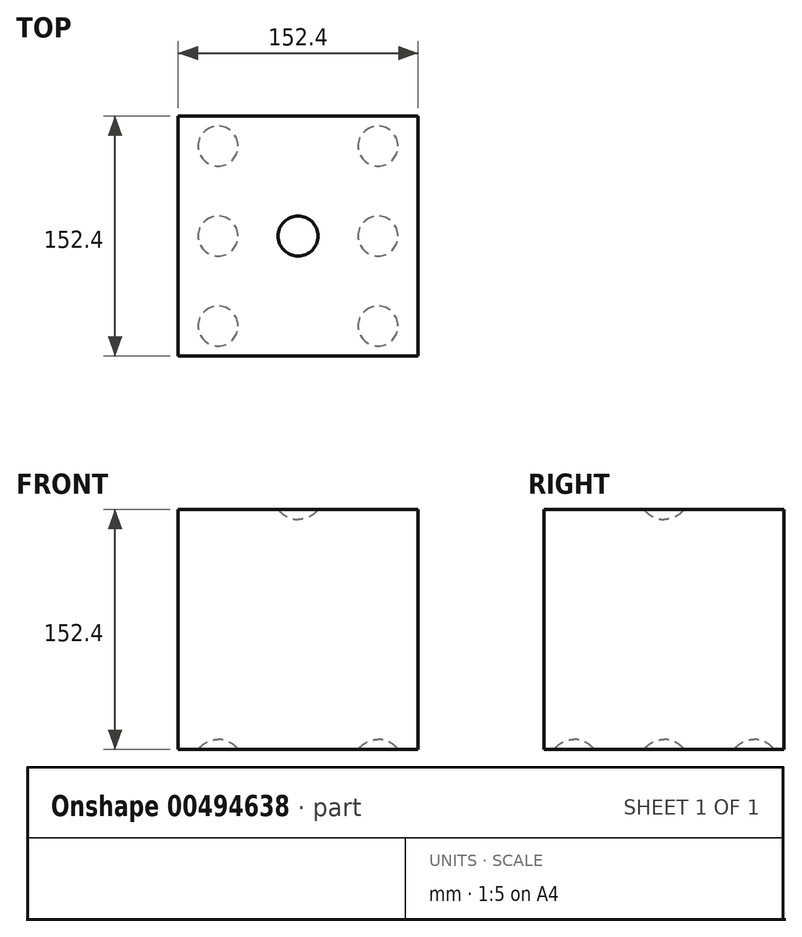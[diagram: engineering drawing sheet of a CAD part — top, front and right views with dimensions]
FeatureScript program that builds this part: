
annotation { "Feature Type Name" : "Feature", "Feature Type Description" : "" }
export const myFeature = defineFeature(function(context is Context, id is Id, definition is map)
    precondition{}
    {
        {
            var Q0;
            Q0=qCreatedBy(makeId("Front.planeOp"),FACE);
            var sketch = newSketch(context, id + "F0", { "sketchPlane" : qUnion([Q0])});
            skLineSegment(sketch, "E0.bottom", {"start": v(76.2, 76.2) * mm, "end": v(-76.2, 76.2) * mm});
            skLineSegment(sketch, "E0.top", {"start": v(76.2, -76.2) * mm, "end": v(-76.2, -76.2) * mm});
            skLineSegment(sketch, "E0.left", {"start": v(76.2, 76.2) * mm, "end": v(76.2, -76.2) * mm});
            skLineSegment(sketch, "E0.right", {"start": v(-76.2, 76.2) * mm, "end": v(-76.2, -76.2) * mm});
            skPoint(sketch, "E0.middle", {"position": v(0, 0) * mm});
            skSolve(sketch);
        }
        {
            var Q0;
            Q0=makeQuery(id+"F0.imprint","IMPRINT",FACE,{"disambiguationData":[TD([[makeQuery(id+"F0.imprint","IMPRINT",EDGE,{"derivedFrom":sQuery(id+"F0.wireOp",EDGE,"E0.bottom")}),1.0]])]});
            extrude(context, id + "F1", {"entities" : qUnion([Q0]), "depth" : 152.4 * mm});
        }
        {
            var Q0;
            Q0=makeQuery(id+"F1.opExtrude","SWEPT_FACE",FACE,{"disambiguationData":[OSD([sQuery(id+"F0.wireOp",EDGE,"E0.bottom")])]});
            var sketch = newSketch(context, id + "F2", { "sketchPlane" : qUnion([Q0])});
            skCircle(sketch, "E1", {"center": v(0, -76.2) * mm, "radius": 12.7 * mm});
            skPoint(sketch, "E1.centerSnap0", {"position": v(76.2, -76.2) * mm});
            skSolve(sketch);
        }
        {
            var Q0;
            Q0=makeQuery(id+"F2.imprint","IMPRINT",FACE,{"disambiguationData":[TD([[makeQuery(id+"F2.imprint","IMPRINT",EDGE,{"derivedFrom":sQuery(id+"F2.wireOp",EDGE,"E1")}),1.0]])]});
            extrude(context, id + "F3", {"entities" : qUnion([Q0]), "operationType" : NewBodyOperationType.REMOVE, "oppositeDirection" : true, "depth" : 6.35 * mm});
        }
        {
            var Q0;
            Q0=makeQuery(id+"F3.boolean.opBoolean","COPY",EDGE,{"derivedFrom":makeQuery(id+"F3.opExtrude","CAP_EDGE",EDGE,{"disambiguationData":[OSD([sQuery(id+"F2.wireOp",EDGE,"E1")])],"isStart":false})});
            fillet(context, id + "F4", {"entities" : qUnion([Q0]), "radius" : 15.85 * mm, "tangentPropagation" : true, "allowEdgeOverflow" : false});
        }
        {
            var Q0;
            Q0=makeQuery(id+"F1.opExtrude","SWEPT_FACE",FACE,{"disambiguationData":[OSD([sQuery(id+"F0.wireOp",EDGE,"E0.top")])]});
            var sketch = newSketch(context, id + "F5", { "sketchPlane" : qUnion([Q0])});
            skCircle(sketch, "E2", {"center": v(50.8, 76.2) * mm, "radius": 12.7 * mm});
            skCircle(sketch, "E3", {"center": v(50.8, 133.35) * mm, "radius": 12.7 * mm});
            skCircle(sketch, "E4", {"center": v(50.8, 19.05) * mm, "radius": 12.7 * mm});
            skCircle(sketch, "E5", {"center": v(-50.8, 19.05) * mm, "radius": 12.7 * mm});
            skCircle(sketch, "E6", {"center": v(-50.8, 76.2) * mm, "radius": 12.7 * mm});
            skCircle(sketch, "E7", {"center": v(-50.8, 133.35) * mm, "radius": 12.7 * mm});
            skSolve(sketch);
        }
        {
            var Q0;
            Q0=makeQuery(id+"F5.imprint","IMPRINT",FACE,{"disambiguationData":[TD([[makeQuery(id+"F5.imprint","IMPRINT",EDGE,{"derivedFrom":sQuery(id+"F5.wireOp",EDGE,"E4")}),1.0]])]});
            var Q1;
            Q1=makeQuery(id+"F5.imprint","IMPRINT",FACE,{"disambiguationData":[TD([[makeQuery(id+"F5.imprint","IMPRINT",EDGE,{"derivedFrom":sQuery(id+"F5.wireOp",EDGE,"E2")}),1.0]])]});
            var Q2;
            Q2=makeQuery(id+"F5.imprint","IMPRINT",FACE,{"disambiguationData":[TD([[makeQuery(id+"F5.imprint","IMPRINT",EDGE,{"derivedFrom":sQuery(id+"F5.wireOp",EDGE,"E5")}),1.0]])]});
            var Q3;
            Q3=makeQuery(id+"F5.imprint","IMPRINT",FACE,{"disambiguationData":[TD([[makeQuery(id+"F5.imprint","IMPRINT",EDGE,{"derivedFrom":sQuery(id+"F5.wireOp",EDGE,"E6")}),1.0]])]});
            var Q4;
            Q4=makeQuery(id+"F5.imprint","IMPRINT",FACE,{"disambiguationData":[TD([[makeQuery(id+"F5.imprint","IMPRINT",EDGE,{"derivedFrom":sQuery(id+"F5.wireOp",EDGE,"E7")}),1.0]])]});
            var Q5;
            Q5=makeQuery(id+"F5.imprint","IMPRINT",FACE,{"disambiguationData":[TD([[makeQuery(id+"F5.imprint","IMPRINT",EDGE,{"derivedFrom":sQuery(id+"F5.wireOp",EDGE,"E3")}),1.0]])]});
            extrude(context, id + "F6", {"entities" : qUnion([Q0, Q1, Q2, Q3, Q4, Q5]), "operationType" : NewBodyOperationType.REMOVE, "oppositeDirection" : true, "depth" : 6.35 * mm});
        }
        {
            var Q0;
            Q0=makeQuery(id+"F6.boolean.opBoolean","COPY",EDGE,{"derivedFrom":makeQuery(id+"F6.opExtrude","CAP_EDGE",EDGE,{"disambiguationData":[OSD([sQuery(id+"F5.wireOp",EDGE,"E4")])],"isStart":false})});
            var Q1;
            Q1=makeQuery(id+"F6.boolean.opBoolean","COPY",EDGE,{"derivedFrom":makeQuery(id+"F6.opExtrude","CAP_EDGE",EDGE,{"disambiguationData":[OSD([sQuery(id+"F5.wireOp",EDGE,"E2")])],"isStart":false})});
            var Q2;
            Q2=makeQuery(id+"F6.boolean.opBoolean","COPY",EDGE,{"derivedFrom":makeQuery(id+"F6.opExtrude","CAP_EDGE",EDGE,{"disambiguationData":[OSD([sQuery(id+"F5.wireOp",EDGE,"E3")])],"isStart":false})});
            var Q3;
            Q3=makeQuery(id+"F6.boolean.opBoolean","COPY",EDGE,{"derivedFrom":makeQuery(id+"F6.opExtrude","CAP_EDGE",EDGE,{"disambiguationData":[OSD([sQuery(id+"F5.wireOp",EDGE,"E5")])],"isStart":false})});
            var Q4;
            Q4=makeQuery(id+"F6.boolean.opBoolean","COPY",EDGE,{"derivedFrom":makeQuery(id+"F6.opExtrude","CAP_EDGE",EDGE,{"disambiguationData":[OSD([sQuery(id+"F5.wireOp",EDGE,"E6")])],"isStart":false})});
            var Q5;
            Q5=makeQuery(id+"F6.boolean.opBoolean","COPY",EDGE,{"derivedFrom":makeQuery(id+"F6.opExtrude","CAP_EDGE",EDGE,{"disambiguationData":[OSD([sQuery(id+"F5.wireOp",EDGE,"E7")])],"isStart":false})});
            fillet(context, id + "F7", {"entities" : qUnion([Q0, Q1, Q2, Q3, Q4, Q5]), "radius" : 15.85 * mm, "tangentPropagation" : true, "allowEdgeOverflow" : false});
        }
        {
            var Q0;
            Q0=makeQuery(id+"F1.opExtrude","CAP_FACE",FACE,{"disambiguationData":[OSD([sQuery(id+"F0.wireOp",EDGE,"E0.bottom"),sQuery(id+"F0.wireOp",EDGE,"E0.top"),sQuery(id+"F0.wireOp",EDGE,"E0.left"),sQuery(id+"F0.wireOp",EDGE,"E0.right")])],"isStart":true});
            var sketch = newSketch(context, id + "F8", { "sketchPlane" : qUnion([Q0])});
            skCircle(sketch, "E8", {"center": v(-50.8, 57.15) * mm, "radius": 12.7 * mm});
            skCircle(sketch, "E9", {"center": v(50.8, 57.15) * mm, "radius": 12.7 * mm});
            skCircle(sketch, "E10", {"center": v(50.8, -57.15) * mm, "radius": 12.7 * mm});
            skCircle(sketch, "E11", {"center": v(-50.8, -57.15) * mm, "radius": 12.7 * mm});
            skSolve(sketch);
        }
        {
            var Q0;
            Q0=makeQuery(id+"F8.imprint","IMPRINT",FACE,{"disambiguationData":[TD([[makeQuery(id+"F8.imprint","IMPRINT",EDGE,{"derivedFrom":sQuery(id+"F8.wireOp",EDGE,"E10")}),1.0]])]});
            var Q1;
            Q1=makeQuery(id+"F8.imprint","IMPRINT",FACE,{"disambiguationData":[TD([[makeQuery(id+"F8.imprint","IMPRINT",EDGE,{"derivedFrom":sQuery(id+"F8.wireOp",EDGE,"E11")}),1.0]])]});
            var Q2;
            Q2=makeQuery(id+"F8.imprint","IMPRINT",FACE,{"disambiguationData":[TD([[makeQuery(id+"F8.imprint","IMPRINT",EDGE,{"derivedFrom":sQuery(id+"F8.wireOp",EDGE,"E8")}),1.0]])]});
            var Q3;
            Q3=makeQuery(id+"F8.imprint","IMPRINT",FACE,{"disambiguationData":[TD([[makeQuery(id+"F8.imprint","IMPRINT",EDGE,{"derivedFrom":sQuery(id+"F8.wireOp",EDGE,"E9")}),1.0]])]});
            extrude(context, id + "F9", {"entities" : qUnion([Q0, Q1, Q2, Q3]), "operationType" : NewBodyOperationType.ADD, "oppositeDirection" : true, "depth" : 6.35 * mm});
        }
    });
